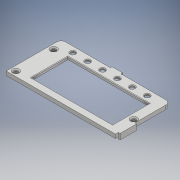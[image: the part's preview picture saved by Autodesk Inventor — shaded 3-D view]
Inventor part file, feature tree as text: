
AUTODESK INVENTOR PART (.ipt)
format: ipt  version: 2017 (Build 210142000, 142)  size: 291,840 bytes
history: native  units: mm
features: extrude x7, sketch x7, projected_geometry x3, fillet x2, chamfer x1
ambient origin geometry x8: Origin, YZ Plane, XZ Plane, XY Plane, X Axis, Y Axis, Z Axis, Center Point
bodies: Solid1 (feature_tree)
feature tree (20):
  extrude  "Extrusion1"  Depth=48.0mm
  extrude  "edge"  Depth=86.0mm
  extrude  "Extrusion3"  Depth=8.5mm
  sketch  "Sketch4"  dims[d9=15.25mm d12=60.0mm d14=13.0mm d15=10.0mm d17=10.0mm]
  extrude  "Extrusion4"  Depth=10.0mm
  extrude  "Extrusion5"  Depth=81.0mm
  chamfer  "Chamfer1"  Distance=1.4mm
  fillet  "Fillet1"  Radius=1.0mm
  fillet  "Fillet2"  Radius=2.0mm
  extrude  "Extrusion6"  Depth=1.0mm
  extrude  "Extrusion7"  Depth=3.5mm
  sketch  "Sketch1"  dims[d0=95.5mm d1=48.0mm]
  sketch  "Sketch2"  dims[d2=4.0mm d3=86.0mm]
  projected_geometry  "Projected Loop1"
  sketch  "Sketch3"  dims[d6=16.0mm d8=8.5mm]
  projected_geometry  "Projected Loop2"
  sketch  "Sketch5"  dims[d19=4.0mm d20=81.0mm d21=1.4mm d22=0.0mm d23=1.0mm d24=2.0mm d25=0.0mm]
  sketch  "Sketch6"  dims[d26=1.0mm d27=1.0mm]
  sketch  "Sketch7"  dims[d28=1.0mm d29=3.5mm d30=33.0mm d31=10.75mm d32=4.25mm d33=3.25mm d35=28.75mm d36=1.5mm d37=0.0mm d38=7.0mm d39=7.0mm d40=7.0mm d41=1.5mm d42=2.0mm d43=3.5mm d44=1.0mm d45=3.0mm d46=2.0mm d47=0.0mm d48=2.0mm d49=0.0mm d50=1.2mm d51=2.0mm d52=45.0deg d53=0.5mm d54=1.0mm d55=1.5mm d56=9.5mm d57=1.5mm d58=31.0mm d59=14.5mm d60=5.0mm d61=0.0mm d63=1.0mm d64=1.0mm d65=0.0mm d66=10.0mm d67=6.0mm]
  projected_geometry  "Projected Loop3"
